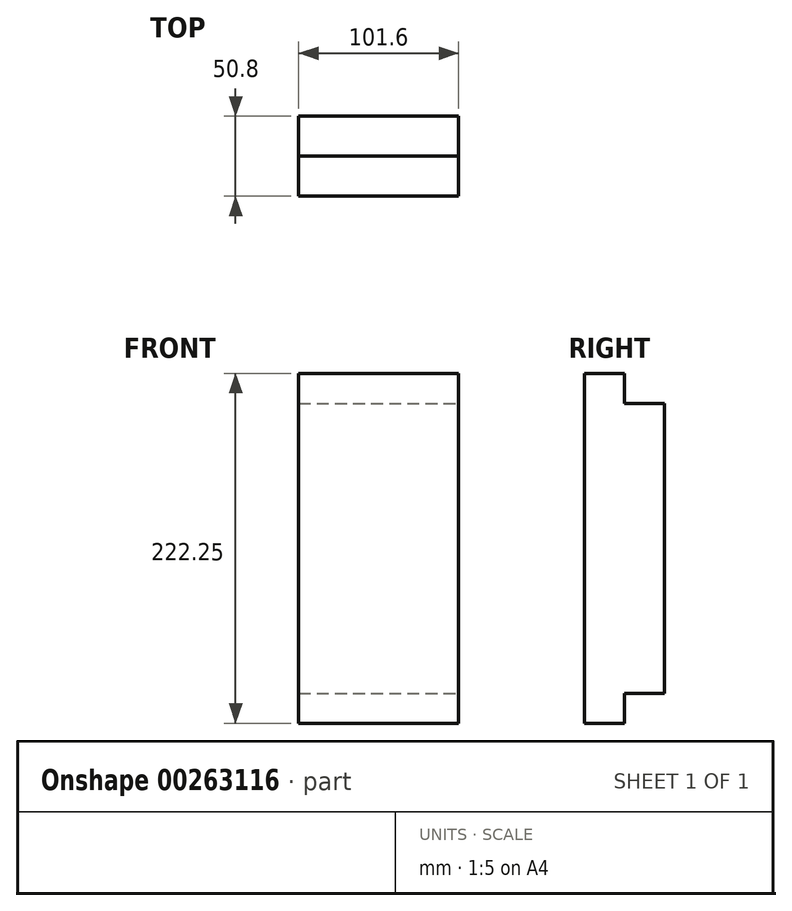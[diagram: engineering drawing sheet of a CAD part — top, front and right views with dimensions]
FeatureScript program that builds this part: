
annotation { "Feature Type Name" : "Feature", "Feature Type Description" : "" }
export const myFeature = defineFeature(function(context is Context, id is Id, definition is map)
    precondition{}
    {
        {
            var Q0;
            Q0=qCreatedBy(makeId("Top.planeOp"),FACE);
            var sketch = newSketch(context, id + "F0", { "sketchPlane" : qUnion([Q0])});
            skLineSegment(sketch, "E0.bottom", {"start": v(50.8, 25.4) * mm, "end": v(-50.8, 25.4) * mm});
            skLineSegment(sketch, "E0.top", {"start": v(50.8, -25.4) * mm, "end": v(-50.8, -25.4) * mm});
            skLineSegment(sketch, "E0.left", {"start": v(50.8, 25.4) * mm, "end": v(50.8, -25.4) * mm});
            skLineSegment(sketch, "E0.right", {"start": v(-50.8, 25.4) * mm, "end": v(-50.8, -25.4) * mm});
            skPoint(sketch, "E0.middle", {"position": v(0, 0) * mm});
            skSolve(sketch);
        }
        {
            var Q0;
            Q0=qSketchRegion(id+"F0",true);
            extrude(context, id + "F1", {"entities" : qUnion([Q0]), "depth" : 184.15 * mm});
        }
        {
            var Q0;
            Q0=makeQuery(id+"F1.opExtrude","SWEPT_FACE",FACE,{"disambiguationData":[OSD([sQuery(id+"F0.wireOp",EDGE,"E0.left")])]});
            var sketch = newSketch(context, id + "F2", { "sketchPlane" : qUnion([Q0])});
            skLineSegment(sketch, "E1.bottom", {"start": v(-25.4, 0) * mm, "end": v(0, 0) * mm});
            skLineSegment(sketch, "E1.top", {"start": v(-25.4, -19.05) * mm, "end": v(0, -19.05) * mm});
            skLineSegment(sketch, "E1.left", {"start": v(-25.4, 0) * mm, "end": v(-25.4, -19.05) * mm});
            skLineSegment(sketch, "E1.right", {"start": v(0, 0) * mm, "end": v(0, -19.05) * mm});
            skLineSegment(sketch, "E2.bottom", {"start": v(-25.4, 184.15) * mm, "end": v(0, 184.15) * mm});
            skLineSegment(sketch, "E2.top", {"start": v(-25.4, 203.2) * mm, "end": v(0, 203.2) * mm});
            skLineSegment(sketch, "E2.left", {"start": v(-25.4, 184.15) * mm, "end": v(-25.4, 203.2) * mm});
            skLineSegment(sketch, "E2.right", {"start": v(0, 184.15) * mm, "end": v(0, 203.2) * mm});
            skSolve(sketch);
        }
        {
            var Q0;
            Q0 = qSketchRegion(id + "F2", true);
            var Q1;
            Q1=makeQuery(id+"F1.opExtrude","SWEPT_FACE",FACE,{"disambiguationData":[OSD([sQuery(id+"F0.wireOp",EDGE,"E0.right")])]});
            extrude(context, id + "F3", {"entities" : qUnion([Q0]), "operationType" : NewBodyOperationType.ADD, "endBound" : BoundingType.UP_TO_SURFACE, "oppositeDirection" : true, "endBoundEntityFace" : qUnion([Q1]), "depth" : 25.4 * mm});
        }
    });
